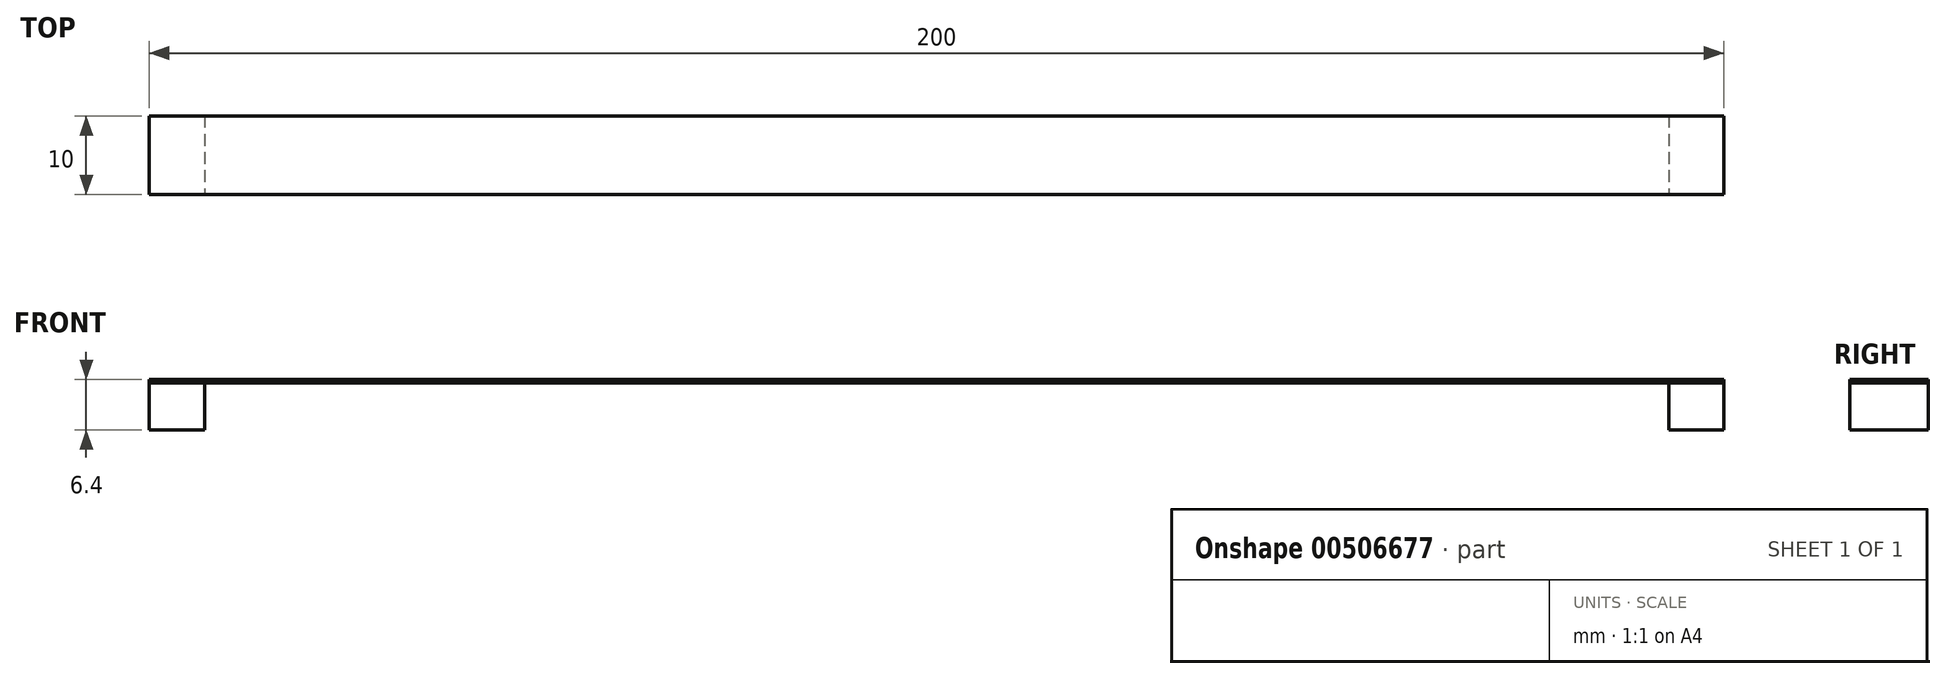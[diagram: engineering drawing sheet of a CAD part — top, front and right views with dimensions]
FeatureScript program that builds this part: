
annotation { "Feature Type Name" : "Feature", "Feature Type Description" : "" }
export const myFeature = defineFeature(function(context is Context, id is Id, definition is map)
    precondition{}
    {
        {
            var Q0;
            Q0=qCreatedBy(makeId("Top.planeOp"),FACE);
            var sketch = newSketch(context, id + "F0", { "sketchPlane" : qUnion([Q0])});
            skLineSegment(sketch, "E0.bottom", {"start": v(-100, 0) * mm, "end": v(-93, 0) * mm});
            skLineSegment(sketch, "E0.top", {"start": v(-100, -10) * mm, "end": v(-93, -10) * mm});
            skLineSegment(sketch, "E0.left", {"start": v(-100, 0) * mm, "end": v(-100, -10) * mm});
            skLineSegment(sketch, "E0.right", {"start": v(-93, 0) * mm, "end": v(-93, -10) * mm});
            skLineSegment(sketch, "E1.MirrorCS", {"start": v(100, 0) * mm, "end": v(100, -10) * mm});
            skLineSegment(sketch, "E2.MirrorCS", {"start": v(100, -10) * mm, "end": v(93, -10) * mm});
            skLineSegment(sketch, "E3.MirrorCS", {"start": v(93, 0) * mm, "end": v(93, -10) * mm});
            skLineSegment(sketch, "E4.MirrorCS", {"start": v(100, 0) * mm, "end": v(93, 0) * mm});
            skLineSegment(sketch, "E5.bottom", {"start": v(-100, 0) * mm, "end": v(100, 0) * mm});
            skLineSegment(sketch, "E5.top", {"start": v(-100, -10) * mm, "end": v(100, -10) * mm});
            skSolve(sketch);
        }
        {
            var Q0;
            {var subQ0=sQuery(id+"F0.wireOp",EDGE,"E0.right");Q0=makeQuery(id+"F0.imprint","IMPRINT",FACE,{"disambiguationData":[TD([[makeQuery(id+"F0.imprint","IMPRINT",EDGE,{"derivedFrom":subQ0}),-1.0]])]});}
            var Q1;
            {var subQ0=sQuery(id+"F0.wireOp",EDGE,"E3.MirrorCS");Q1=makeQuery(id+"F0.imprint","IMPRINT",FACE,{"disambiguationData":[TD([[makeQuery(id+"F0.imprint","IMPRINT",EDGE,{"derivedFrom":subQ0}),1.0]])]});}
            extrude(context, id + "F1", {"entities" : qUnion([Q0, Q1]), "oppositeDirection" : true, "depth" : 6 * mm});
        }
        {
            var Q0;
            Q0 = qSketchRegion(id + "F0", true);
            extrude(context, id + "F2", {"entities" : qUnion([Q0]), "depth" : 0.4 * mm});
        }
    });
